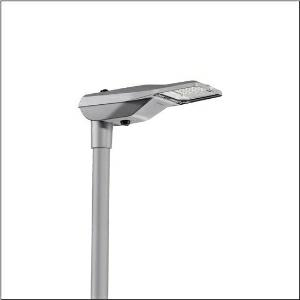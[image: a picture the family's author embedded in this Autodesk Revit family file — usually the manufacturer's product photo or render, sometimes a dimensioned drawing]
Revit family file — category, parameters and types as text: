
# Revit family: streetlight_sl_21_iq_micro___st1_5a_5xe1p31y08cb_38f8
name_source: partatom
category: Lighting Fixtures
units: mm (PartAtom-declared; Revit-internal decimal feet)

## family parameters
Cut with Voids When Loaded = No
Host = Face
Light Source = No
Part Type = Normal
Room Calculation Point = No
Round Connector Dimension = Use Diameter
Shared = No

## types (1)
- --- (1 x LED, 2840 lm, 19.1 W, 3000K)
    Apparent Load = 19 VA
    CIE Flux Codes = 22 53 95 100 100
    Color Rendering = 70
    Color Temperature = 3000K
    Default Elevation = 1800 mm
    Description = Streetlight SL 21 iQ micro, mast luminaire, primary light control with lens, of PMMA, primary optical cover: cover, of toughened safety glass, transparent, light distribution: ST1.5a, light emission: direct distribution, primary light characteristic: asymmetric, installation type: post-top, side-entry, LED, High Power LED, rated luminous flux: 2.840lm, luminous efficacy: 149lm/W, light colour: 730, colour temperature: 3000K, control gear: iQ-Street Remote, D4i with power reduction, control: pre-setting: logarithmic dimming characteristic, Street-Remote, Auto-Match, Temp-Guard, Lumen-Switch, Night-Set, Smart-Wire, Light-Fading, Desk-Remote (wireless, voltage-free reading and setting of iQ features in the workshop via application-optimized NFC function/RFID function), optimised constant luminous flux control (CLO 2.0), mains connection: 220..240V, AC, 50/60Hz, start of lifetime: 19W, end of service life: 20W, reduction: 9W, luminaire housing, of diecast aluminium, powder-coated, SITECO metallic grey (DB 702S), corrosivity category C5 high according to DIN EN ISO 12944, please order mast flange separately, inclination adjustable: 0°, 5°, 10°, 15°, sealing non-destructively replaceable, multi-level sealing system, length: 528mm, width: 235mm, height: 110mm, mast flange for spigot size: 42mm (side-entry): 5XC10008XM4, 60/48mm (side-entry/post-top): 5XC10108XM2, 76/60mm (side-entry/post-top): 5XC10108XM1, mounting height: 4..8m, Smart Interface below and above, protection rating (complete): IP66, insulation class (complete): insulation class II (safety insulation), certification: CE, ENEC, ENEC+, VDE, impact resistance: IK10, permissible operating ambient temperature for outdoor applications: -40..+50°C, standard-compliant lighting for roads and squares, packaging unit: 1 piece

Light Distribution: ST1.5a
    Height = 110 mm
    Lamp = 1 x LED
    Lamp Light Flux = 2840 lm
    Lamp Power = 19.1 W
    Lamp count = 1
    Length = 528 mm
    Luminous efficacy = 149 lm/W
    Manufacturer = Siteco
    ModVariant = No
    Model = 5XE1P31Y08CB
    Number of Poles = 1
    OnlyDefault = Yes
    Power Factor = 1
    Product Name = Streetlight SL 21 iQ micro | ST1.5a
    Product group = mast luminaire | pylon top
    ProductGroupID = 6100
    Protection Class = Protection class II
    Protection Degree = IP 66
    RLX_Detail_Level = 1
    RLX_Emergency_Light_Flux = 0 lm
    RLX_Emergency_Type = 0
    RLX_Emergency_Type_DB = No
    RlxData = <blob elided: 102937 chars, md5=2b78e38d>
    Socket = socket
    Standby Power = 0 W
    System Light Flux = 2840 lm
    System Power = 19 W
    Type Comments = factory setting: luminous flux: 100 % | dim-lin: 254 | 387 mA
    Type Image = l_1007239.jpg
    URL = http://relux.com
    VarID = @adj_111967
    Voltage = 0 V
    Weight = 0.00 kg
    Width = 235 mm

## geometry (parser evidence)
native form markers: Blend x4, Sweep x11
no freeform markers — native parametric forms only
